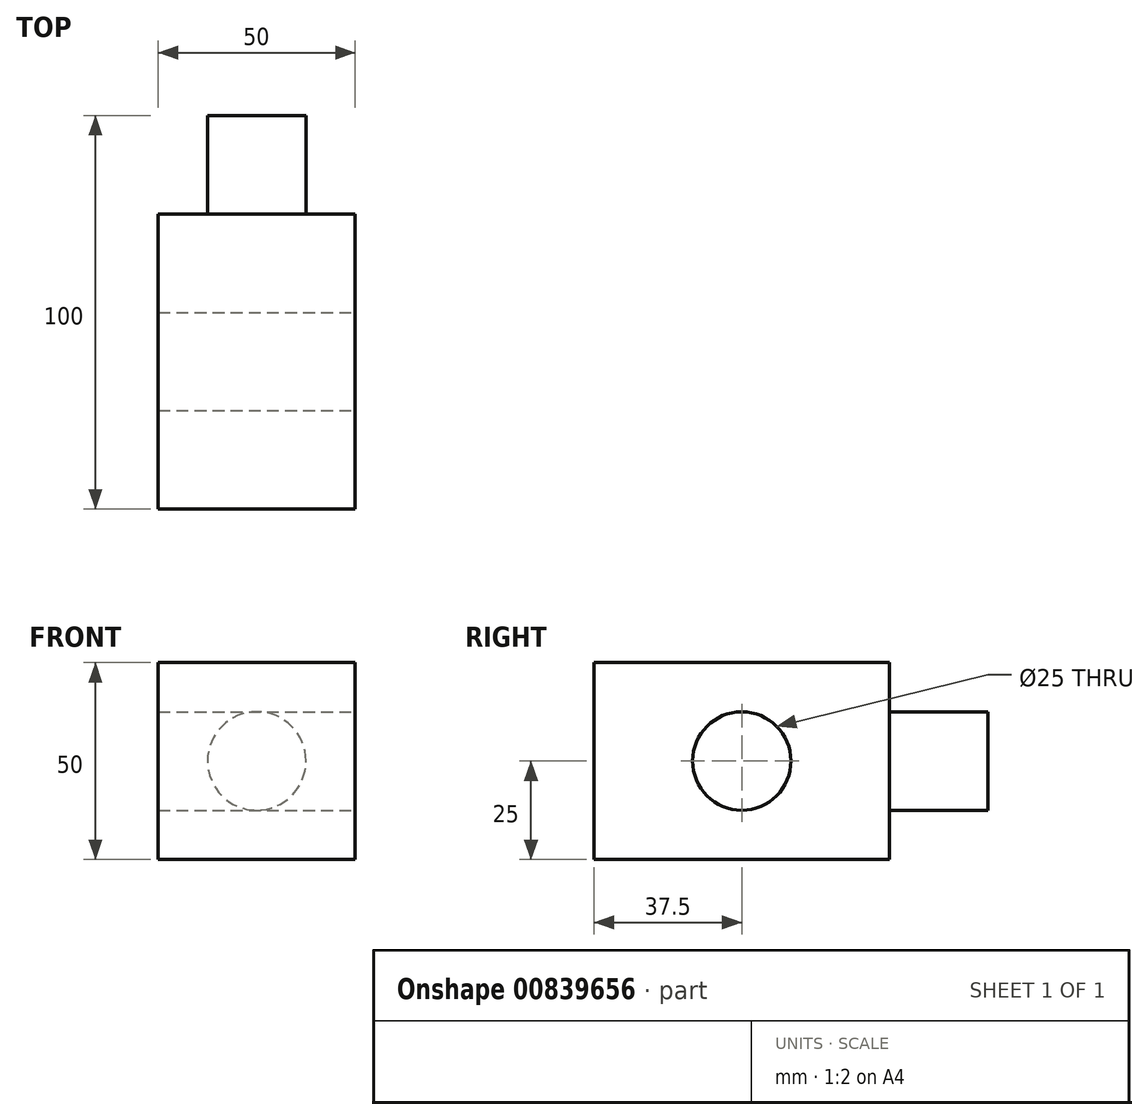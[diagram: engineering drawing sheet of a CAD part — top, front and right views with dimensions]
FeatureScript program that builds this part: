
annotation { "Feature Type Name" : "Feature", "Feature Type Description" : "" }
export const myFeature = defineFeature(function(context is Context, id is Id, definition is map)
    precondition{}
    {
        {
            var Q0;
            Q0=qCreatedBy(makeId("Front.planeOp"),FACE);
            var sketch = newSketch(context, id + "F0", { "sketchPlane" : qUnion([Q0])});
            skCircle(sketch, "E0", {"center": v(0, 0) * mm, "radius": 12.5 * mm});
            skSolve(sketch);
        }
        {
            var Q0;
            Q0=makeQuery(id+"F0.imprint","IMPRINT",FACE,{"disambiguationData":[TD([[makeQuery(id+"F0.imprint","IMPRINT",EDGE,{"derivedFrom":sQuery(id+"F0.wireOp",EDGE,"E0")}),1.0]])]});
            extrude(context, id + "F1", {"entities" : qUnion([Q0]), "depth" : 25 * mm, "offsetDistance" : 25 * mm});
        }
        {
            var Q0;
            Q0=makeQuery(id+"F1.opExtrude","CAP_FACE",FACE,{"disambiguationData":[OSD([sQuery(id+"F0.wireOp",EDGE,"E0")])],"isStart":false});
            var sketch = newSketch(context, id + "F2", { "sketchPlane" : qUnion([Q0])});
            skLineSegment(sketch, "E1.bottom", {"start": v(-25, 25) * mm, "end": v(25, 25) * mm});
            skLineSegment(sketch, "E1.top", {"start": v(-25, -25) * mm, "end": v(25, -25) * mm});
            skLineSegment(sketch, "E1.left", {"start": v(-25, 25) * mm, "end": v(-25, -25) * mm});
            skLineSegment(sketch, "E1.right", {"start": v(25, 25) * mm, "end": v(25, -25) * mm});
            skLineSegment(sketch, "E2", {"start": v(-25, -25) * mm, "end": v(25, 25) * mm, "construction": true});
            skLineSegment(sketch, "E3", {"start": v(25, -25) * mm, "end": v(-25, 25) * mm, "construction": true});
            skPoint(sketch, "E4", {"position": v(0, 0) * mm});
            skSolve(sketch);
        }
        {
            var Q0;
            Q0=makeQuery(id+"F2.imprint","IMPRINT",FACE,{"disambiguationData":[TD([[makeQuery(id+"F2.imprint","IMPRINT",EDGE,{"derivedFrom":sQuery(id+"F2.wireOp",EDGE,"E1.bottom")}),-1.0]])]});
            var Q1;
            Q1=makeQuery(id+"F2.imprint","IMPRINT",FACE,{"disambiguationData":[TD([[makeQuery(id+"F2.imprint","IMPRINT",EDGE,{"derivedFrom":makeQuery(id+"F1.opExtrude","CAP_EDGE",EDGE,{"disambiguationData":[OSD([sQuery(id+"F0.wireOp",EDGE,"E0")])],"isStart":false})}),1.0]])]});
            extrude(context, id + "F3", {"entities" : qUnion([Q0, Q1]), "operationType" : NewBodyOperationType.ADD, "depth" : 75 * mm, "offsetDistance" : 25 * mm});
        }
        {
            var Q0;
            Q0=makeQuery(id+"F3.opExtrude","SWEPT_FACE",FACE,{"disambiguationData":[OSD([sQuery(id+"F2.wireOp",EDGE,"E1.right")])]});
            var sketch = newSketch(context, id + "F4", { "sketchPlane" : qUnion([Q0])});
            skCircle(sketch, "E5", {"center": v(-62.5, 0) * mm, "radius": 12.5 * mm});
            skSolve(sketch);
        }
        {
            var Q0;
            Q0=makeQuery(id+"F4.imprint","IMPRINT",FACE,{"disambiguationData":[TD([[makeQuery(id+"F4.imprint","IMPRINT",EDGE,{"derivedFrom":sQuery(id+"F4.wireOp",EDGE,"E5")}),1.0]])]});
            extrude(context, id + "F5", {"entities" : qUnion([Q0]), "operationType" : NewBodyOperationType.REMOVE, "endBound" : BoundingType.THROUGH_ALL, "oppositeDirection" : true, "depth" : 25 * mm, "offsetDistance" : 25 * mm});
        }
    });
